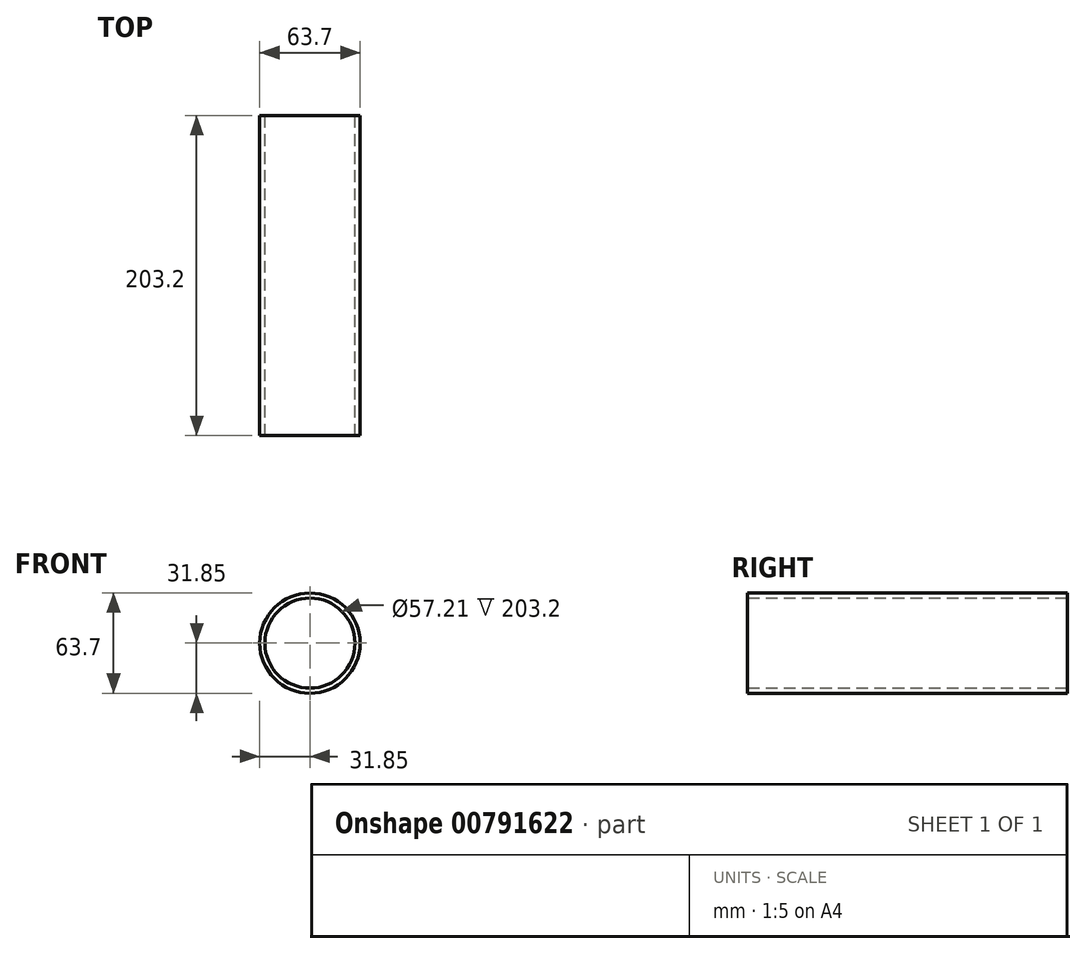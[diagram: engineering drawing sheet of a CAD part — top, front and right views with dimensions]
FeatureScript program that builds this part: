
annotation { "Feature Type Name" : "Feature", "Feature Type Description" : "" }
export const myFeature = defineFeature(function(context is Context, id is Id, definition is map)
    precondition{}
    {
        {
            var Q0;
            Q0=qCreatedBy(makeId("Front.planeOp"),FACE);
            var sketch = newSketch(context, id + "F0", { "sketchPlane" : qUnion([Q0])});
            skCircle(sketch, "E0", {"center": v(0, 0) * mm, "radius": 31.85 * mm});
            skCircle(sketch, "E1", {"center": v(0, 0) * mm, "radius": 28.6 * mm});
            skSolve(sketch);
        }
        {
            var Q0;
            Q0=makeQuery(id+"F0.imprint","IMPRINT",FACE,{"disambiguationData":[TD([[makeQuery(id+"F0.imprint","IMPRINT",EDGE,{"derivedFrom":sQuery(id+"F0.wireOp",EDGE,"E0")}),1.0]])]});
            extrude(context, id + "F1", {"entities" : qUnion([Q0]), "depth" : 203.2 * mm, "offsetDistance" : 25.4 * mm});
        }
    });
